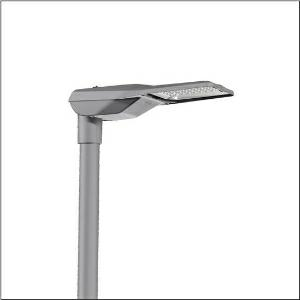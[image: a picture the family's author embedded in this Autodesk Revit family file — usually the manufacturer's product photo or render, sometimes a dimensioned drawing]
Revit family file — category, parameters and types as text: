
# Revit family: streetlight_sl_21_mini___st0_5a_5xe2b43s08hb_1e61
name_source: partatom
category: Lighting Fixtures
units: mm (PartAtom-declared; Revit-internal decimal feet)

## family parameters
Cut with Voids When Loaded = No
Host = Face
Light Source = No
Part Type = Normal
Room Calculation Point = No
Round Connector Dimension = Use Diameter
Shared = No

## types (1)
- --- (1 x LED, 9430 lm, 66 W, 4000K)
    Apparent Load = 66 VA
    CIE Flux Codes = 41 75 97 100 100
    Color Rendering = 70
    Color Temperature = 4000K
    Default Elevation = 1800 mm
    Description = Streetlight SL 21 mini, mast luminaire, primary light control with lens, of PMMA, primary optical cover: cover, of toughened safety glass, transparent, light distribution: ST0.5a, light emission: direct distribution, primary light characteristic: asymmetric, installation type: side-entry, post-top, LED, High Power LED, rated luminous flux: 9.430lm, luminous efficacy: 143lm/W, light colour: 740, colour temperature: 4000K, control gear: D4i, control: overheat protection, constant luminous flux control, time-dependent luminous flux control, flexible luminous flux parameterisation, pre-setting: logarithmic dimming characteristic, mains connection: 220..240V, AC, 50/60Hz, start of lifetime: 66W, end of service life: 69W, reduction: 30W, luminaire housing, of diecast aluminium, powder-coated, Siteco® metallic grey (DB 702S), corrosivity category C5 mid according to DIN EN ISO 12944, please order mast flange separately, inclination adjustable: 0°, 5°, 10°, 15°, sealing non-destructively replaceable, multi-level sealing system, length: 628mm, width: 235mm, height: 110mm, mast flange for spigot size: 42mm (side-entry): 5XC10008XM4, 60/48mm (side-entry/post-top): 5XC10108XM2, 76/60mm (side-entry/post-top): 5XC10108XM1, mounting height: 4..8m, Smart Interface above, protection rating (complete): IP66, insulation class (complete): insulation class II (safety insulation), certification: CE, ENEC, ENEC+, VDE, impact resistance: IK10, permissible operating ambient temperature for outdoor applications: -40..+50°C, standard-compliant lighting for roads and squares, packaging unit: 1 piece

Light Distribution: ST0.5a
    Height = 110 mm
    Lamp = 1 x LED
    Lamp Light Flux = 9430 lm
    Lamp Power = 66 W
    Lamp count = 1
    Length = 625 mm
    Luminous efficacy = 143 lm/W
    Manufacturer = Siteco
    ModVariant = No
    Model = 5XE2B43S08HB
    Number of Poles = 1
    OnlyDefault = Yes
    Power Factor = 1
    Product Name = Streetlight SL 21 mini | ST0.5a
    Product group = mast luminaire | pylon top
    ProductGroupID = 6100
    Protection Class = Protection class II
    Protection Degree = IP 66
    RLX_Detail_Level = 1
    RLX_Emergency_Light_Flux = 0 lm
    RLX_Emergency_Type = 0
    RLX_Emergency_Type_DB = No
    RlxData = <blob elided: 37101 chars, md5=0ff82f3e>
    Socket = socket
    Standby Power = 0 W
    System Light Flux = 9430 lm
    System Power = 66 W
    Type Comments = factory setting: luminous flux: 100 % | dim-lin: 254 | 670 mA
    Type Image = l_1003515.jpg
    URL = http://relux.com
    VarID = @adj_191150
    Voltage = 0 V
    Weight = 0.00 kg
    Width = 234 mm

## geometry (parser evidence)
native form markers: Blend x4, Sweep x12
no freeform markers — native parametric forms only
